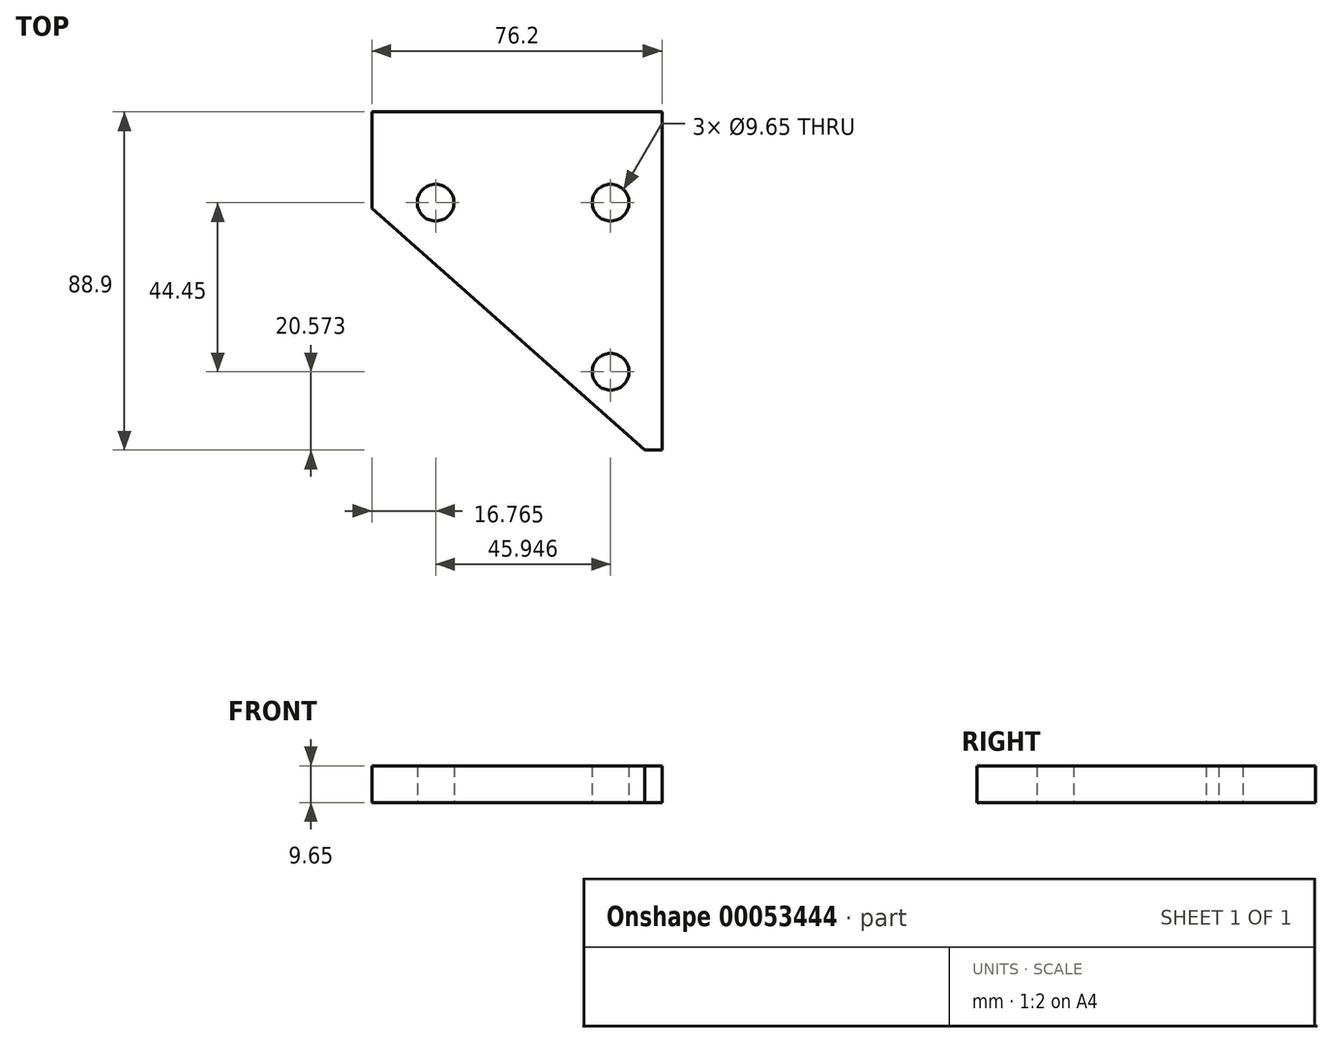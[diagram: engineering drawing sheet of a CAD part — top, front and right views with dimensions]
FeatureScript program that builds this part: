
annotation { "Feature Type Name" : "Feature", "Feature Type Description" : "" }
export const myFeature = defineFeature(function(context is Context, id is Id, definition is map)
    precondition{}
    {
        {
            var Q0;
            Q0=qCreatedBy(makeId("Top.planeOp"),FACE);
            var sketch = newSketch(context, id + "F0", { "sketchPlane" : qUnion([Q0])});
            skLineSegment(sketch, "E0", {"start": v(26.85, -10.34) * mm, "end": v(31.42, -10.34) * mm});
            skLineSegment(sketch, "E1", {"start": v(31.42, -10.34) * mm, "end": v(31.42, 78.56) * mm});
            skLineSegment(sketch, "E2", {"start": v(31.42, 78.56) * mm, "end": v(-44.78, 78.56) * mm});
            skLineSegment(sketch, "E3", {"start": v(-44.78, 78.56) * mm, "end": v(-44.78, 53.16) * mm});
            skLineSegment(sketch, "E4", {"start": v(-44.78, 53.16) * mm, "end": v(26.85, -10.34) * mm});
            skCircle(sketch, "E5", {"center": v(-28.01, 54.68) * mm, "radius": 4.83 * mm});
            skCircle(sketch, "E6", {"center": v(17.93, 54.68) * mm, "radius": 4.83 * mm});
            skCircle(sketch, "E7", {"center": v(17.93, 10.23) * mm, "radius": 4.83 * mm});
            skSolve(sketch);
        }
        {
            var Q0;
            Q0=makeQuery(id+"F0.imprint","IMPRINT",FACE,{"disambiguationData":[TD([[makeQuery(id+"F0.imprint","IMPRINT",EDGE,{"derivedFrom":sQuery(id+"F0.wireOp",EDGE,"E0")}),1.0]])]});
            extrude(context, id + "F1", {"entities" : qUnion([Q0]), "depth" : 9.65 * mm});
        }
    });
